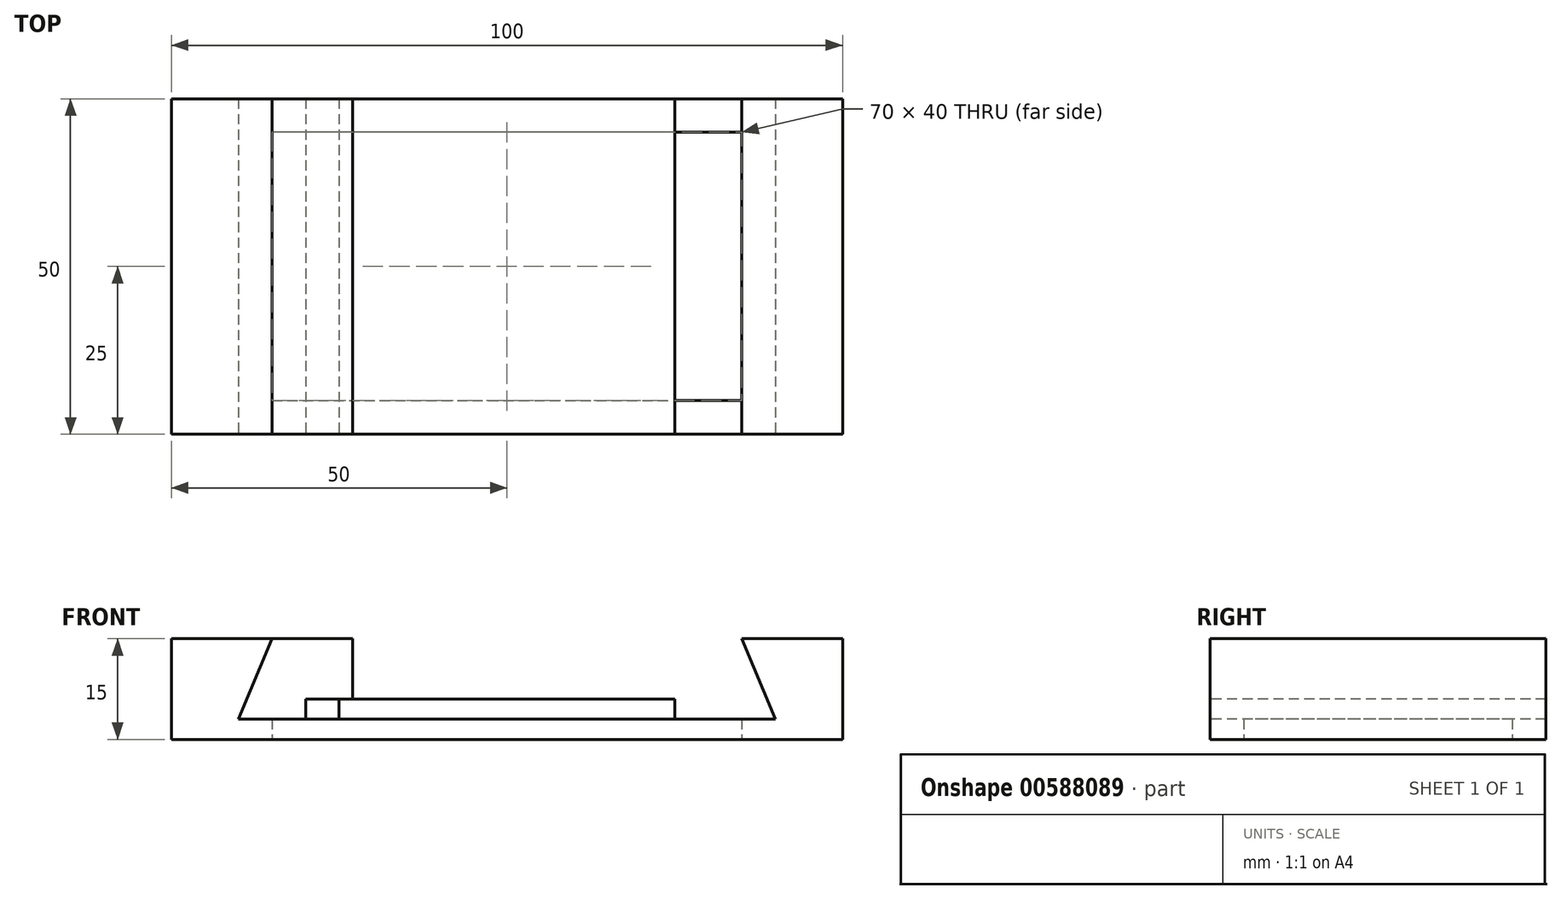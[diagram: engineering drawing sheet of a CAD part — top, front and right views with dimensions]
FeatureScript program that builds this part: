
annotation { "Feature Type Name" : "Feature", "Feature Type Description" : "" }
export const myFeature = defineFeature(function(context is Context, id is Id, definition is map)
    precondition{}
    {
        {
            var Q0;
            Q0=qCreatedBy(makeId("Top.planeOp"),FACE);
            var sketch = newSketch(context, id + "F0", { "sketchPlane" : qUnion([Q0])});
            skLineSegment(sketch, "E0.bottom", {"start": v(50, -25) * mm, "end": v(-50, -25) * mm});
            skLineSegment(sketch, "E0.top", {"start": v(50, 25) * mm, "end": v(-50, 25) * mm});
            skLineSegment(sketch, "E0.left", {"start": v(50, -25) * mm, "end": v(50, 25) * mm});
            skLineSegment(sketch, "E0.right", {"start": v(-50, -25) * mm, "end": v(-50, 25) * mm});
            skPoint(sketch, "E0.middle", {"position": v(0, 0) * mm});
            skLineSegment(sketch, "E1", {"start": v(-40, 25) * mm, "end": v(-40, -25) * mm});
            skLineSegment(sketch, "E2", {"start": v(40, 25) * mm, "end": v(40, -25) * mm});
            skLineSegment(sketch, "E3", {"start": v(-35, 25) * mm, "end": v(-35, -25) * mm});
            skLineSegment(sketch, "E4", {"start": v(35, 25) * mm, "end": v(35, -25) * mm});
            skLineSegment(sketch, "E5", {"start": v(-35, -20) * mm, "end": v(35, -20) * mm});
            skLineSegment(sketch, "E6", {"start": v(35, 20) * mm, "end": v(-35, 20) * mm});
            skLineSegment(sketch, "E7", {"start": v(0, -25) * mm, "end": v(0, 25) * mm, "construction": true});
            skSolve(sketch);
        }
        {
            var Q0;
            Q0=makeQuery(id+"F0.imprint","IMPRINT",FACE,{"disambiguationData":[TD([[makeQuery(id+"F0.imprint","IMPRINT",EDGE,{"derivedFrom":sQuery(id+"F0.wireOp",EDGE,"E0.bottom")}),-1.0]])]});
            var Q1;
            {var subQ4=sQuery(id+"F0.wireOp",EDGE,"E1");Q1=makeQuery(id+"F0.imprint","IMPRINT",FACE,{"disambiguationData":[TD([[makeQuery(id+"F0.imprint","IMPRINT",EDGE,{"derivedFrom":subQ4}),1.0]])]});}
            var Q2;
            {var subQ5=sQuery(id+"F0.wireOp",EDGE,"E6");Q2=makeQuery(id+"F0.imprint","IMPRINT",FACE,{"disambiguationData":[TD([[makeQuery(id+"F0.imprint","IMPRINT",EDGE,{"derivedFrom":subQ5}),-1.0]])]});}
            var Q3;
            {var subQ4=sQuery(id+"F0.wireOp",EDGE,"E2");Q3=makeQuery(id+"F0.imprint","IMPRINT",FACE,{"disambiguationData":[TD([[makeQuery(id+"F0.imprint","IMPRINT",EDGE,{"derivedFrom":subQ4}),-1.0]])]});}
            extrude(context, id + "F1", {"entities" : qUnion([Q0, Q1, Q2, Q3]), "depth" : 3 * mm, "offsetDistance" : 25 * mm});
        }
        {
            var Q0;
            {var subQ0=sQuery(id+"F0.wireOp",EDGE,"E1");Q0=makeQuery(id+"F0.imprint","IMPRINT",FACE,{"disambiguationData":[TD([[makeQuery(id+"F0.imprint","IMPRINT",EDGE,{"derivedFrom":subQ0}),1.0]])]});}
            var Q1;
            {var subQ0=sQuery(id+"F0.wireOp",EDGE,"E0.right");Q1=makeQuery(id+"F0.imprint","IMPRINT",FACE,{"disambiguationData":[TD([[makeQuery(id+"F0.imprint","IMPRINT",EDGE,{"derivedFrom":subQ0}),-1.0]])]});}
            var Q2;
            {var subQ0=sQuery(id+"F0.wireOp",EDGE,"E2");Q2=makeQuery(id+"F0.imprint","IMPRINT",FACE,{"disambiguationData":[TD([[makeQuery(id+"F0.imprint","IMPRINT",EDGE,{"derivedFrom":subQ0}),-1.0]])]});}
            var Q3;
            {var subQ0=sQuery(id+"F0.wireOp",EDGE,"E0.left");Q3=makeQuery(id+"F0.imprint","IMPRINT",FACE,{"disambiguationData":[TD([[makeQuery(id+"F0.imprint","IMPRINT",EDGE,{"derivedFrom":subQ0}),1.0]])]});}
            extrude(context, id + "F2", {"entities" : qUnion([Q0, Q1, Q2, Q3]), "operationType" : NewBodyOperationType.ADD, "depth" : 15 * mm, "offsetDistance" : 25 * mm});
        }
        {
            var Q0;
            {var subQ0=sQuery(id+"F0.wireOp",EDGE,"E0.bottom");var subQ1=makeQuery(id+"F0.imprint","INTERSECT",VERTEX,{"derivedFrom":[subQ0,sQuery(id+"F0.wireOp",EDGE,"E1")]});var subQ2=makeQuery(id+"F0.imprint","INTERSECT",VERTEX,{"derivedFrom":[subQ0,sQuery(id+"F0.wireOp",EDGE,"E2")]});Q0=makeQuery(id+"F2.boolean.opBoolean","MERGE",FACE,{"derivedFrom":[makeQuery(id+"F1.opExtrude","SWEPT_FACE",FACE,{"disambiguationData":[OSD([subQ0])]}),makeQuery(id+"F2.opExtrude","SWEPT_FACE",FACE,{"disambiguationData":[OSD([subQ0]),TDD([makeQuery(id+"F0.imprint","IMPRINT",EDGE,{"disambiguationData":[TD([[makeQuery(id+"F0.imprint","INTERSECT",VERTEX,{"derivedFrom":[subQ0,sQuery(id+"F0.wireOp",EDGE,"E0.left")]}),-1.0]])],"derivedFrom":subQ0}),makeQuery(id+"F0.imprint","IMPRINT",EDGE,{"disambiguationData":[TD([[subQ2,-1.0]])],"derivedFrom":subQ0})])]}),makeQuery(id+"F2.opExtrude","SWEPT_FACE",FACE,{"disambiguationData":[OSD([subQ0]),TDD([makeQuery(id+"F0.imprint","IMPRINT",EDGE,{"disambiguationData":[TD([[subQ1,1.0]])],"derivedFrom":subQ0}),makeQuery(id+"F0.imprint","IMPRINT",EDGE,{"disambiguationData":[TD([[makeQuery(id+"F0.imprint","INTERSECT",VERTEX,{"derivedFrom":[subQ0,sQuery(id+"F0.wireOp",EDGE,"E0.right")]}),1.0]])],"derivedFrom":subQ0})])]})]});}
            var sketch = newSketch(context, id + "F3", { "sketchPlane" : qUnion([Q0])});
            skLineSegment(sketch, "E8.0", {"start": v(-35, 15) * mm, "end": v(-35, 3) * mm});
            skLineSegment(sketch, "E8.1", {"start": v(-35, 15) * mm, "end": v(-50, 15) * mm});
            skLineSegment(sketch, "E8.3", {"start": v(35, 15) * mm, "end": v(35, 3) * mm});
            skLineSegment(sketch, "E8.4", {"start": v(35, 3) * mm, "end": v(-35, 3) * mm});
            skLineSegment(sketch, "E8.5", {"start": v(50, 15) * mm, "end": v(35, 15) * mm});
            skLineSegment(sketch, "E8.6", {"start": v(50, 15) * mm, "end": v(50, 0) * mm});
            skLineSegment(sketch, "E8.7", {"start": v(-50, 15) * mm, "end": v(-50, 0) * mm});
            skPoint(sketch, "E8.2.end.orphan", {"position": v(-50, 0) * mm});
            skPoint(sketch, "E8.2.start.orphan", {"position": v(50, 0) * mm});
            skLineSegment(sketch, "E9", {"start": v(-35, 3) * mm, "end": v(-50, 3) * mm});
            skPoint(sketch, "E10.0", {"position": v(-35, 0) * mm});
            skPoint(sketch, "E11.0", {"position": v(-40, 0) * mm});
            skPoint(sketch, "E12.0", {"position": v(35, 0) * mm});
            skPoint(sketch, "E13.0", {"position": v(40, 0) * mm});
            skLineSegment(sketch, "E14", {"start": v(-40, 3) * mm, "end": v(-40, 15) * mm});
            skLineSegment(sketch, "E15", {"start": v(-35, 15) * mm, "end": v(-40, 3) * mm});
            skLineSegment(sketch, "E16", {"start": v(35, 3) * mm, "end": v(50, 3) * mm});
            skLineSegment(sketch, "E17", {"start": v(40, 3) * mm, "end": v(40, 15) * mm});
            skLineSegment(sketch, "E18", {"start": v(35, 15) * mm, "end": v(40, 3) * mm});
            skSolve(sketch);
        }
        {
            var Q0;
            {var subQ0=sQuery(id+"F3.wireOp",EDGE,"E8.0");Q0=makeQuery(id+"F3.imprint","IMPRINT",FACE,{"disambiguationData":[TD([[makeQuery(id+"F3.imprint","IMPRINT",EDGE,{"derivedFrom":subQ0}),-1.0]])]});}
            var Q1;
            {var subQ0=sQuery(id+"F3.wireOp",EDGE,"E8.3");Q1=makeQuery(id+"F3.imprint","IMPRINT",FACE,{"disambiguationData":[TD([[makeQuery(id+"F3.imprint","IMPRINT",EDGE,{"derivedFrom":subQ0}),1.0]])]});}
            extrude(context, id + "F4", {"entities" : qUnion([Q0, Q1]), "operationType" : NewBodyOperationType.REMOVE, "endBound" : BoundingType.THROUGH_ALL, "oppositeDirection" : true, "depth" : 25 * mm, "offsetDistance" : 25 * mm});
        }
        {
            var Q0;
            {var subQ0=sQuery(id+"F0.wireOp",EDGE,"E0.bottom");var subQ1=makeQuery(id+"F0.imprint","INTERSECT",VERTEX,{"derivedFrom":[subQ0,sQuery(id+"F0.wireOp",EDGE,"E1")]});var subQ2=makeQuery(id+"F0.imprint","INTERSECT",VERTEX,{"derivedFrom":[subQ0,sQuery(id+"F0.wireOp",EDGE,"E2")]});Q0=makeQuery(id+"F2.boolean.opBoolean","MERGE",FACE,{"derivedFrom":[makeQuery(id+"F1.opExtrude","SWEPT_FACE",FACE,{"disambiguationData":[OSD([subQ0])]}),makeQuery(id+"F2.opExtrude","SWEPT_FACE",FACE,{"disambiguationData":[OSD([subQ0]),TDD([makeQuery(id+"F0.imprint","IMPRINT",EDGE,{"disambiguationData":[TD([[makeQuery(id+"F0.imprint","INTERSECT",VERTEX,{"derivedFrom":[subQ0,sQuery(id+"F0.wireOp",EDGE,"E0.left")]}),-1.0]])],"derivedFrom":subQ0}),makeQuery(id+"F0.imprint","IMPRINT",EDGE,{"disambiguationData":[TD([[subQ2,-1.0]])],"derivedFrom":subQ0})])]}),makeQuery(id+"F2.opExtrude","SWEPT_FACE",FACE,{"disambiguationData":[OSD([subQ0]),TDD([makeQuery(id+"F0.imprint","IMPRINT",EDGE,{"disambiguationData":[TD([[subQ1,1.0]])],"derivedFrom":subQ0}),makeQuery(id+"F0.imprint","IMPRINT",EDGE,{"disambiguationData":[TD([[makeQuery(id+"F0.imprint","INTERSECT",VERTEX,{"derivedFrom":[subQ0,sQuery(id+"F0.wireOp",EDGE,"E0.right")]}),1.0]])],"derivedFrom":subQ0})])]})]});}
            var sketch = newSketch(context, id + "F5", { "sketchPlane" : qUnion([Q0])});
            skLineSegment(sketch, "E19.0", {"start": v(-35, 15) * mm, "end": v(-40, 3) * mm});
            skLineSegment(sketch, "E19.1", {"start": v(40, 3) * mm, "end": v(-40, 3) * mm});
            skLineSegment(sketch, "E19.2", {"start": v(35, 15) * mm, "end": v(40, 3) * mm});
            skPoint(sketch, "E20.0", {"position": v(-35, 0) * mm});
            skPoint(sketch, "E21.0", {"position": v(35, 0) * mm});
            skLineSegment(sketch, "E22", {"start": v(-25, 6) * mm, "end": v(25, 6) * mm});
            skLineSegment(sketch, "E23", {"start": v(-25, 3) * mm, "end": v(-25, 6) * mm});
            skLineSegment(sketch, "E24", {"start": v(25, 3) * mm, "end": v(25, 6) * mm});
            skLineSegment(sketch, "E25", {"start": v(-35, 15) * mm, "end": v(35, 15) * mm, "construction": true});
            skLineSegment(sketch, "E26", {"start": v(-25, 6) * mm, "end": v(-38.75, 6) * mm, "construction": true});
            skLineSegment(sketch, "E27", {"start": v(25, 6) * mm, "end": v(38.75, 6) * mm, "construction": true});
            skPoint(sketch, "E28", {"position": v(-30, 0) * mm});
            skPoint(sketch, "E29", {"position": v(30, 0) * mm});
            skLineSegment(sketch, "E30", {"start": v(-25, 6) * mm, "end": v(-23, 6) * mm});
            skLineSegment(sketch, "E31", {"start": v(-23, 15) * mm, "end": v(-35, 15) * mm});
            skLineSegment(sketch, "E32", {"start": v(-40, 3) * mm, "end": v(-30, 3) * mm});
            skLineSegment(sketch, "E33", {"start": v(-30, 3) * mm, "end": v(-30, 6) * mm});
            skLineSegment(sketch, "E34", {"start": v(-30, 6) * mm, "end": v(-25, 6) * mm});
            skLineSegment(sketch, "E35", {"start": v(-23, 6) * mm, "end": v(-23, 15) * mm});
            skLineSegment(sketch, "E36", {"start": v(0, 0) * mm, "end": v(0, 16.27) * mm, "construction": true});
            skPoint(sketch, "E36.endSnap0", {"position": v(0, 15) * mm});
            skSolve(sketch);
        }
        {
            var Q0;
            Q0=makeQuery(id+"F5.imprint","IMPRINT",FACE,{"disambiguationData":[TD([[makeQuery(id+"F5.imprint","IMPRINT",EDGE,{"derivedFrom":sQuery(id+"F5.wireOp",EDGE,"E22")}),-1.0]])]});
            var Q1;
            {var subQ0=sQuery(id+"F0.wireOp",EDGE,"E0.top");var subQ1=makeQuery(id+"F0.imprint","INTERSECT",VERTEX,{"derivedFrom":[subQ0,sQuery(id+"F0.wireOp",EDGE,"E1")]});var subQ2=makeQuery(id+"F0.imprint","INTERSECT",VERTEX,{"derivedFrom":[subQ0,sQuery(id+"F0.wireOp",EDGE,"E2")]});Q1=makeQuery(id+"F2.boolean.opBoolean","MERGE",FACE,{"derivedFrom":[makeQuery(id+"F1.opExtrude","SWEPT_FACE",FACE,{"disambiguationData":[OSD([subQ0])]}),makeQuery(id+"F2.opExtrude","SWEPT_FACE",FACE,{"disambiguationData":[OSD([subQ0]),TDD([makeQuery(id+"F0.imprint","IMPRINT",EDGE,{"disambiguationData":[TD([[makeQuery(id+"F0.imprint","INTERSECT",VERTEX,{"derivedFrom":[subQ0,sQuery(id+"F0.wireOp",EDGE,"E0.left")]}),-1.0]])],"derivedFrom":subQ0}),makeQuery(id+"F0.imprint","IMPRINT",EDGE,{"disambiguationData":[TD([[subQ2,-1.0]])],"derivedFrom":subQ0})])]}),makeQuery(id+"F2.opExtrude","SWEPT_FACE",FACE,{"disambiguationData":[OSD([subQ0]),TDD([makeQuery(id+"F0.imprint","IMPRINT",EDGE,{"disambiguationData":[TD([[subQ1,1.0]])],"derivedFrom":subQ0}),makeQuery(id+"F0.imprint","IMPRINT",EDGE,{"disambiguationData":[TD([[makeQuery(id+"F0.imprint","INTERSECT",VERTEX,{"derivedFrom":[subQ0,sQuery(id+"F0.wireOp",EDGE,"E0.right")]}),1.0]])],"derivedFrom":subQ0})])]})]});}
            extrude(context, id + "F6", {"entities" : qUnion([Q0]), "endBound" : BoundingType.UP_TO_SURFACE, "oppositeDirection" : true, "depth" : 25 * mm, "endBoundEntityFace" : qUnion([Q1]), "offsetDistance" : 25 * mm});
        }
        {
            var Q0;
            Q0=makeQuery(id+"F5.imprint","IMPRINT",FACE,{"disambiguationData":[TD([[makeQuery(id+"F5.imprint","IMPRINT",EDGE,{"derivedFrom":sQuery(id+"F5.wireOp",EDGE,"E19.0")}),1.0]])]});
            var Q1;
            {var subQ0=sQuery(id+"F0.wireOp",EDGE,"E0.top");var subQ1=makeQuery(id+"F0.imprint","INTERSECT",VERTEX,{"derivedFrom":[subQ0,sQuery(id+"F0.wireOp",EDGE,"E1")]});var subQ2=makeQuery(id+"F0.imprint","INTERSECT",VERTEX,{"derivedFrom":[subQ0,sQuery(id+"F0.wireOp",EDGE,"E2")]});Q1=makeQuery(id+"F2.boolean.opBoolean","MERGE",FACE,{"derivedFrom":[makeQuery(id+"F1.opExtrude","SWEPT_FACE",FACE,{"disambiguationData":[OSD([subQ0])]}),makeQuery(id+"F2.opExtrude","SWEPT_FACE",FACE,{"disambiguationData":[OSD([subQ0]),TDD([makeQuery(id+"F0.imprint","IMPRINT",EDGE,{"disambiguationData":[TD([[makeQuery(id+"F0.imprint","INTERSECT",VERTEX,{"derivedFrom":[subQ0,sQuery(id+"F0.wireOp",EDGE,"E0.left")]}),-1.0]])],"derivedFrom":subQ0}),makeQuery(id+"F0.imprint","IMPRINT",EDGE,{"disambiguationData":[TD([[subQ2,-1.0]])],"derivedFrom":subQ0})])]}),makeQuery(id+"F2.opExtrude","SWEPT_FACE",FACE,{"disambiguationData":[OSD([subQ0]),TDD([makeQuery(id+"F0.imprint","IMPRINT",EDGE,{"disambiguationData":[TD([[subQ1,1.0]])],"derivedFrom":subQ0}),makeQuery(id+"F0.imprint","IMPRINT",EDGE,{"disambiguationData":[TD([[makeQuery(id+"F0.imprint","INTERSECT",VERTEX,{"derivedFrom":[subQ0,sQuery(id+"F0.wireOp",EDGE,"E0.right")]}),1.0]])],"derivedFrom":subQ0})])]})]});}
            extrude(context, id + "F7", {"entities" : qUnion([Q0]), "endBound" : BoundingType.UP_TO_SURFACE, "oppositeDirection" : true, "depth" : 25 * mm, "endBoundEntityFace" : qUnion([Q1]), "offsetDistance" : 25 * mm});
        }
    });
